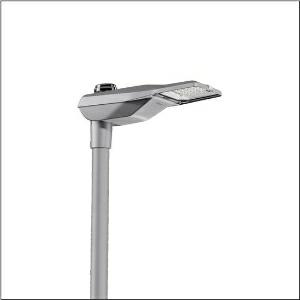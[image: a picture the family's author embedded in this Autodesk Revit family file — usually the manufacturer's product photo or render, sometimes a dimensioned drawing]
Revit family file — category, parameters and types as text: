
# Revit family: streetlight_sl_21_micro___p0_8a_5xe5u47n08db_d803
name_source: partatom
category: Lighting Fixtures
units: mm (PartAtom-declared; Revit-internal decimal feet)

## family parameters
Cut with Voids When Loaded = No
Host = Face
Light Source = No
Part Type = Normal
Room Calculation Point = No
Round Connector Dimension = Use Diameter
Shared = No

## types (1)
- --- (1 x LED, 5250 lm, 39.1 W, 4000K)
    Apparent Load = 39 VA
    CIE Flux Codes = 33 69 96 100 100
    Color Rendering = 70
    Color Temperature = 4000K
    Default Elevation = 1800 mm
    Description = Streetlight SL 21 micro, mast luminaire, primary light control with lens, of PMMA, primary optical cover: cover, of toughened safety glass, transparent, light distribution: P0.8a, light emission: direct distribution, primary light characteristic: asymmetric, installation type: post-top, LED, 3G 1.5mm², High Power LED, rated luminous flux: 5.250lm, luminous efficacy: 134lm/W, light colour: 740, colour temperature: 4000K, control gear: NEMA (7pin), control: flexible luminous flux parameterisation, time-dependent luminous flux control, constant luminous flux control, pre-setting: linear dimming characteristic, overheat protection, mains connection: 230..240V, AC, 50/60Hz, connection cable pre-assembled, cable length: 6,5m, wiring characteristics: H07RN-F, start of lifetime: 39W, end of service life: 41W, reduction: 18W, luminaire housing, of diecast aluminium (EN AC-44300), powder-coated, SITECO metallic grey (DB 702S), corrosivity category C5 high according to DIN EN ISO 12944, multi-level sealing system, sealing non-destructively replaceable, inclination adjustable: 0°, 5°, 10°, 15°, length: 528mm, width: 235mm, height: 110mm, spigot size: 76/60mm (post-top), mounting height: 4..8m, protection rating (complete): IP66, insulation class (complete): insulation class I (protective earthing), certification: CE, ENEC, ENEC+, VDE, impact resistance: IK10, permissible operating ambient temperature for outdoor applications: -40..+50°C, standard-compliant lighting for roads and squares, packaging unit: 1 piece

Light Distribution: P0.8a
    Height = 110 mm
    Lamp = 1 x LED
    Lamp Light Flux = 5250 lm
    Lamp Power = 39.1 W
    Lamp count = 1
    Length = 528 mm
    Luminous efficacy = 134 lm/W
    Manufacturer = Siteco
    ModVariant = No
    Model = 5XE5U47N08DB
    Number of Poles = 1
    OnlyDefault = Yes
    Power Factor = 1
    Product Name = Streetlight SL 21 micro | P0.8a
    Product group = mast luminaire | pylon top
    ProductGroupID = 6100
    Protection Class = Protection class I
    Protection Degree = IP 66
    RLX_Detail_Level = 1
    RLX_Emergency_Light_Flux = 0 lm
    RLX_Emergency_Type = 0
    RLX_Emergency_Type_DB = No
    RlxData = <blob elided: 99061 chars, md5=eb474f8b>
    Socket = socket
    Standby Power = 0 W
    System Light Flux = 5250 lm
    System Power = 39 W
    Type Comments = factory setting: luminous flux: 100 % | dim-lin: 254 | 765 mA
    Type Image = l_1294375.jpg
    URL = http://relux.com
    VarID = @adj_081509
    Voltage = 0 V
    Weight = 0.00 kg
    Width = 235 mm

## geometry (parser evidence)
native form markers: Blend x4, Sweep x10
no freeform markers — native parametric forms only
